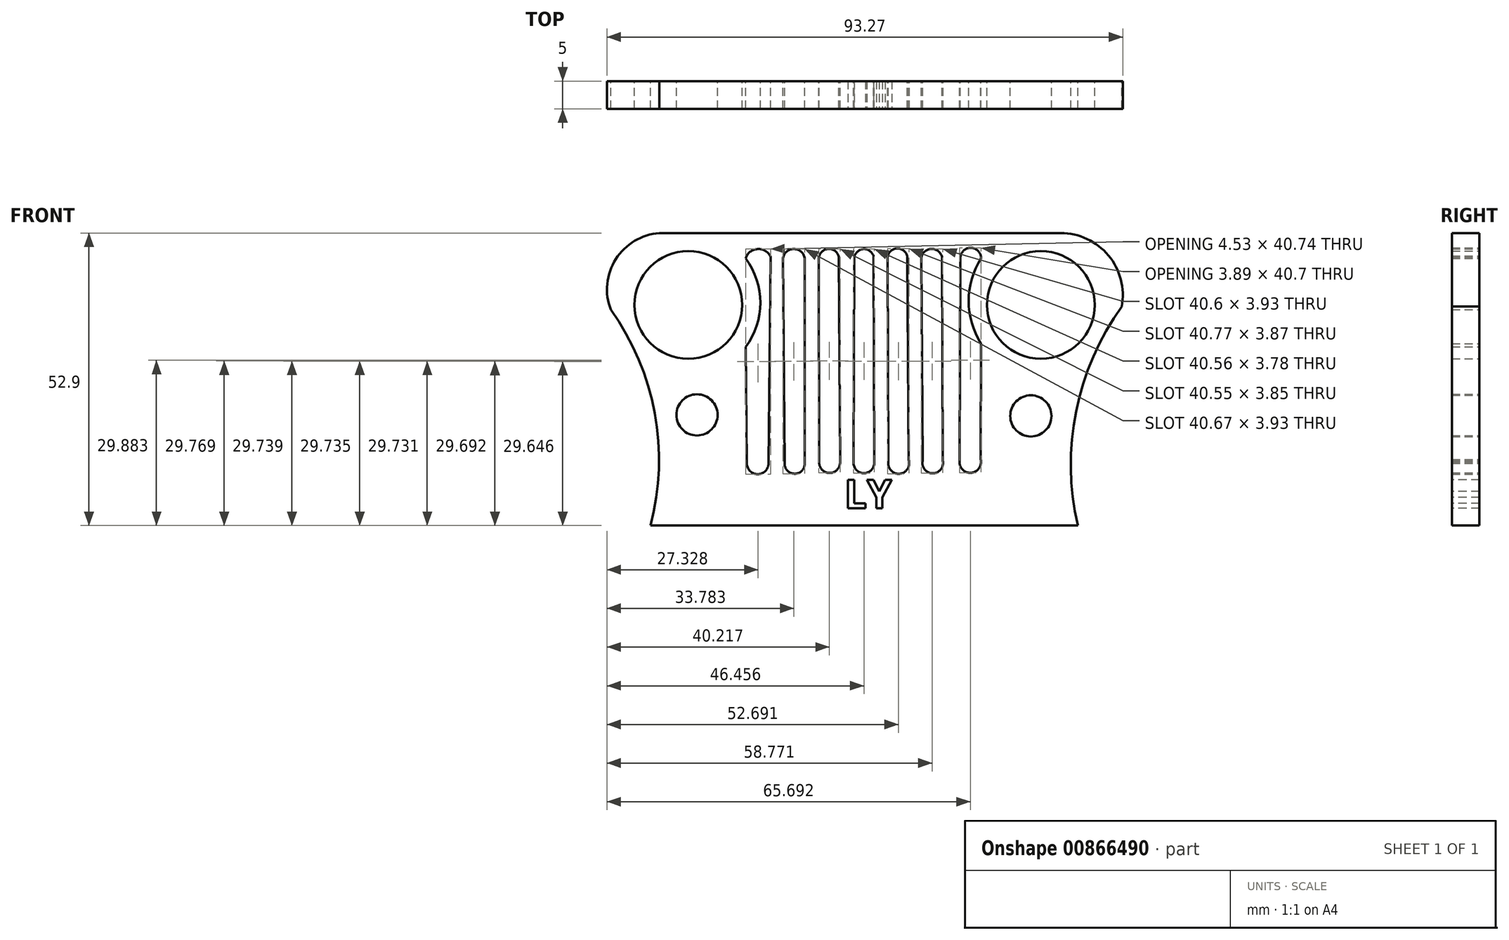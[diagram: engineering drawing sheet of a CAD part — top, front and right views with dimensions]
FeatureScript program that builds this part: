
annotation { "Feature Type Name" : "Feature", "Feature Type Description" : "" }
export const myFeature = defineFeature(function(context is Context, id is Id, definition is map)
    precondition{}
    {
        {
            var Q0;
            Q0=qCreatedBy(makeId("Front.planeOp"),FACE);
            var sketch = newSketch(context, id + "F0", { "sketchPlane" : qUnion([Q0])});
            skArc(sketch, "E0", {"start": v(-37.61, 22.54) * mm, "mid": v(-45.51, 17.82) * mm, "end": v(-46.42, 8.66) * mm});
            skLineSegment(sketch, "E1", {"start": v(-37.61, 22.54) * mm, "end": v(34.94, 22.54) * mm});
            skArc(sketch, "E2", {"start": v(45.98, 9.26) * mm, "mid": v(43.58, 18.49) * mm, "end": v(34.94, 22.54) * mm});
            skArc(sketch, "E3", {"start": v(-39.24, -30.36) * mm, "mid": v(-38.46, -10.05) * mm, "end": v(-46.42, 8.66) * mm});
            skLineSegment(sketch, "E4", {"start": v(-39.24, -30.36) * mm, "end": v(38.03, -30.36) * mm});
            skArc(sketch, "E5", {"start": v(45.98, 9.26) * mm, "mid": v(37.73, -9.7) * mm, "end": v(38.03, -30.36) * mm});
            skCircle(sketch, "E6", {"center": v(-32.4, 9.54) * mm, "radius": 9.74 * mm});
            skCircle(sketch, "E7", {"center": v(31.35, 9.54) * mm, "radius": 9.74 * mm});
            skCircle(sketch, "E8", {"center": v(-30.83, -10.36) * mm, "radius": 3.73 * mm});
            skCircle(sketch, "E9", {"center": v(29.54, -10.54) * mm, "radius": 3.73 * mm});
            skArc(sketch, "E10", {"start": v(-17.5, 18.23) * mm, "mid": v(-19.87, 19.66) * mm, "end": v(-22.04, 17.94) * mm});
            skArc(sketch, "E11", {"start": v(-11.35, 18.04) * mm, "mid": v(-13.32, 19.67) * mm, "end": v(-15.28, 18.04) * mm});
            skArc(sketch, "E12", {"start": v(-5.18, 18.29) * mm, "mid": v(-7.1, 19.68) * mm, "end": v(-8.81, 18.04) * mm});
            skArc(sketch, "E13", {"start": v(1.11, 18.29) * mm, "mid": v(-0.77, 19.65) * mm, "end": v(-2.4, 17.98) * mm});
            skArc(sketch, "E14", {"start": v(7.16, 18.4) * mm, "mid": v(5.33, 19.76) * mm, "end": v(3.65, 18.23) * mm});
            skArc(sketch, "E15", {"start": v(13.46, 18.29) * mm, "mid": v(11.46, 19.68) * mm, "end": v(9.7, 17.98) * mm});
            skArc(sketch, "E16", {"start": v(20.54, 17.98) * mm, "mid": v(18.66, 19.87) * mm, "end": v(16.78, 17.98) * mm});
            skArc(sketch, "E17", {"start": v(-21.81, -19.15) * mm, "mid": v(-19.85, -21.09) * mm, "end": v(-17.89, -19.15) * mm});
            skArc(sketch, "E18", {"start": v(-14.98, -19.1) * mm, "mid": v(-13.09, -21) * mm, "end": v(-11.35, -18.95) * mm});
            skArc(sketch, "E19", {"start": v(-8.73, -19.05) * mm, "mid": v(-6.77, -20.87) * mm, "end": v(-4.96, -18.9) * mm});
            skArc(sketch, "E20", {"start": v(-2.53, -19.1) * mm, "mid": v(-0.57, -20.9) * mm, "end": v(1.24, -18.95) * mm});
            skArc(sketch, "E21", {"start": v(3.76, -18.85) * mm, "mid": v(5.82, -21) * mm, "end": v(7.45, -18.52) * mm});
            skArc(sketch, "E22", {"start": v(9.96, -18.76) * mm, "mid": v(11.9, -20.92) * mm, "end": v(13.6, -18.56) * mm});
            skArc(sketch, "E23", {"start": v(16.65, -18.66) * mm, "mid": v(18.7, -20.83) * mm, "end": v(20.48, -18.42) * mm});
            skLineSegment(sketch, "E24", {"start": v(-15.28, 18.04) * mm, "end": v(-14.98, -19.1) * mm});
            skLineSegment(sketch, "E25", {"start": v(-11.35, 18.04) * mm, "end": v(-11.35, -18.95) * mm});
            skLineSegment(sketch, "E26", {"start": v(-8.81, 18.04) * mm, "end": v(-8.73, -19.05) * mm});
            skLineSegment(sketch, "E27", {"start": v(-5.18, 18.29) * mm, "end": v(-4.96, -18.9) * mm});
            skLineSegment(sketch, "E28", {"start": v(-2.4, 17.98) * mm, "end": v(-2.53, -19.1) * mm});
            skLineSegment(sketch, "E29", {"start": v(1.11, 18.29) * mm, "end": v(1.24, -18.95) * mm});
            skLineSegment(sketch, "E30", {"start": v(3.65, 18.23) * mm, "end": v(3.76, -18.85) * mm});
            skLineSegment(sketch, "E31", {"start": v(7.16, 18.4) * mm, "end": v(7.45, -18.52) * mm});
            skLineSegment(sketch, "E32", {"start": v(9.7, 17.98) * mm, "end": v(9.96, -18.76) * mm});
            skLineSegment(sketch, "E33", {"start": v(13.46, 18.29) * mm, "end": v(13.6, -18.56) * mm});
            skLineSegment(sketch, "E34", {"start": v(16.78, 17.98) * mm, "end": v(16.65, -18.66) * mm});
            skLineSegment(sketch, "E35", {"start": v(-17.5, 18.23) * mm, "end": v(-17.89, -19.15) * mm});
            skArc(sketch, "E36", {"start": v(-22.04, 1.94) * mm, "mid": v(-19.37, 9.94) * mm, "end": v(-22.04, 17.94) * mm});
            skLineSegment(sketch, "E37", {"start": v(-22.04, 1.94) * mm, "end": v(-21.81, -19.15) * mm});
            skArc(sketch, "E38", {"start": v(20.54, 17.98) * mm, "mid": v(18.29, 10.27) * mm, "end": v(20.54, 2.55) * mm});
            skLineSegment(sketch, "E39", {"start": v(20.48, -18.42) * mm, "end": v(20.54, 2.55) * mm});
            skSolve(sketch);
        }
        {
            var Q0;
            Q0 = qSketchRegion(id + "F0", true);
            extrude(context, id + "F1", {"entities" : qUnion([Q0]), "depth" : 5 * mm, "offsetDistance" : 25 * mm});
        }
        {
            var Q0;
            Q0=makeQuery(id+"F1.opExtrude","CAP_FACE",FACE,{"disambiguationData":[OSD([sQuery(id+"F0.wireOp",EDGE,"E0"),sQuery(id+"F0.wireOp",EDGE,"E1"),sQuery(id+"F0.wireOp",EDGE,"E2"),sQuery(id+"F0.wireOp",EDGE,"E3"),sQuery(id+"F0.wireOp",EDGE,"E4"),sQuery(id+"F0.wireOp",EDGE,"E5"),sQuery(id+"F0.wireOp",EDGE,"E6"),sQuery(id+"F0.wireOp",EDGE,"E7"),sQuery(id+"F0.wireOp",EDGE,"E8"),sQuery(id+"F0.wireOp",EDGE,"E9"),sQuery(id+"F0.wireOp",EDGE,"E10"),sQuery(id+"F0.wireOp",EDGE,"E11"),sQuery(id+"F0.wireOp",EDGE,"E12"),sQuery(id+"F0.wireOp",EDGE,"E13"),sQuery(id+"F0.wireOp",EDGE,"E14"),sQuery(id+"F0.wireOp",EDGE,"E15"),sQuery(id+"F0.wireOp",EDGE,"E16"),sQuery(id+"F0.wireOp",EDGE,"E17"),sQuery(id+"F0.wireOp",EDGE,"E18"),sQuery(id+"F0.wireOp",EDGE,"E19"),sQuery(id+"F0.wireOp",EDGE,"E20"),sQuery(id+"F0.wireOp",EDGE,"E21"),sQuery(id+"F0.wireOp",EDGE,"E22"),sQuery(id+"F0.wireOp",EDGE,"E23"),sQuery(id+"F0.wireOp",EDGE,"E24"),sQuery(id+"F0.wireOp",EDGE,"E25"),sQuery(id+"F0.wireOp",EDGE,"E26"),sQuery(id+"F0.wireOp",EDGE,"E27"),sQuery(id+"F0.wireOp",EDGE,"E28"),sQuery(id+"F0.wireOp",EDGE,"E29"),sQuery(id+"F0.wireOp",EDGE,"E30"),sQuery(id+"F0.wireOp",EDGE,"E31"),sQuery(id+"F0.wireOp",EDGE,"E32"),sQuery(id+"F0.wireOp",EDGE,"E33"),sQuery(id+"F0.wireOp",EDGE,"E34"),sQuery(id+"F0.wireOp",EDGE,"E35"),sQuery(id+"F0.wireOp",EDGE,"E36"),sQuery(id+"F0.wireOp",EDGE,"E37"),sQuery(id+"F0.wireOp",EDGE,"E38"),sQuery(id+"F0.wireOp",EDGE,"E39")])],"isStart":false});
            var sketch = newSketch(context, id + "F2", { "sketchPlane" : qUnion([Q0])});
            skText(sketch, "E40", { "text": "LY", "fontName": "OpenSans-Bold.ttf"});
            const initialGuessF2  = {"E40": [-0.00416, -0.02725, 1, 0, 0.00517]};
            skSetInitialGuess(sketch, initialGuessF2);
            skSolve(sketch);
        }
        {
            var Q0;
            Q0 = qSketchRegion(id + "F2", true);
            extrude(context, id + "F3", {"entities" : qUnion([Q0]), "operationType" : NewBodyOperationType.REMOVE, "oppositeDirection" : true, "depth" : 25 * mm, "offsetDistance" : 25 * mm});
        }
    });
